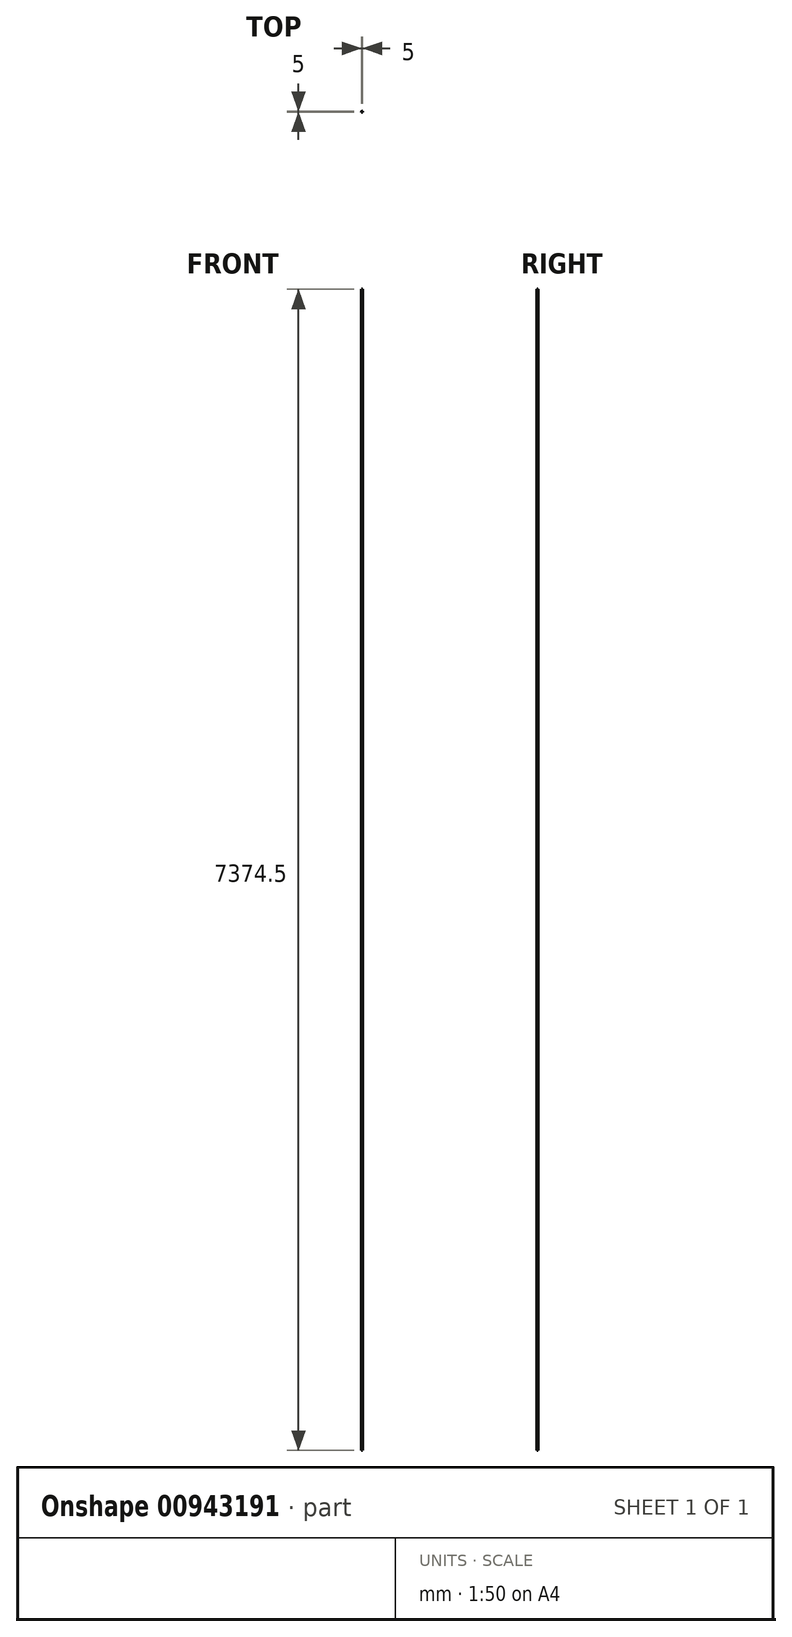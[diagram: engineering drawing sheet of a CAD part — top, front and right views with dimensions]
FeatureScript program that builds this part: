
annotation { "Feature Type Name" : "Feature", "Feature Type Description" : "" }
export const myFeature = defineFeature(function(context is Context, id is Id, definition is map)
    precondition{}
    {
        {
            var Q0;
            Q0=qCreatedBy(makeId("Top.planeOp"),FACE);
            var sketch = newSketch(context, id + "F0", { "sketchPlane" : qUnion([Q0])});
            skCircle(sketch, "E0", {"center": v(0, 0) * mm, "radius": 2.5 * mm});
            skSolve(sketch);
        }
        {
            var Q0;
            Q0=qSketchRegion(id+"F0",true);
            extrude(context, id + "F1", {"entities" : qUnion([Q0]), "depth" : 7374.5 * mm, "offsetDistance" : 25 * mm});
        }
    });
